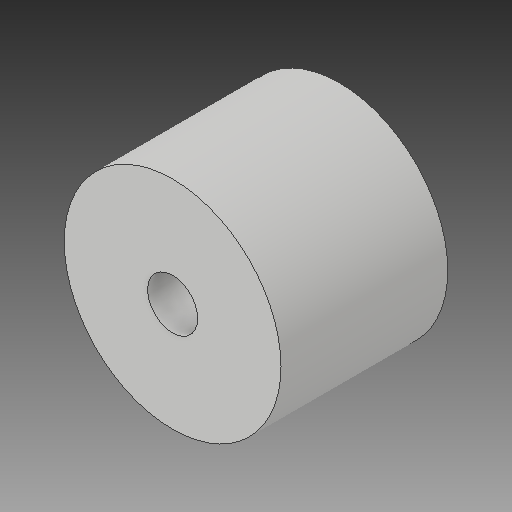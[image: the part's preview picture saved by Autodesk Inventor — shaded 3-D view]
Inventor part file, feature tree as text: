
AUTODESK INVENTOR PART (.ipt)
format: ipt  version: 2019 (Build 230136000, 136)  size: 98,816 bytes
history: native  units: mm
features: extrude x2, sketch x2
ambient origin geometry x8: Origin, YZ Plane, XZ Plane, XY Plane, X Axis, Y Axis, Z Axis, Center Point
bodies: Solid1 (feature_tree)
feature tree (4):
  extrude  "Extrusion1"  Depth=100.0mm TaperAngle=0.0deg
  extrude  "Extrusion2"  Depth=10.0mm TaperAngle=0.0deg
  sketch  "Sketch1"  dims[d0=130.0mm d1=100.0mm d2=0.0mm]
  sketch  "Sketch2"  dims[d3=30.0mm d4=10.0mm d5=0.0mm]
